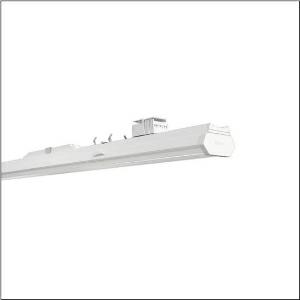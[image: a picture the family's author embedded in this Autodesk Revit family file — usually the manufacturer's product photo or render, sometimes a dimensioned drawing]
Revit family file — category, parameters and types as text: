
# Revit family: licross_21_protected_mo_52td1bvn45xgd
name_source: partatom
category: Lighting Fixtures
units: mm (PartAtom-declared; Revit-internal decimal feet)

## family parameters
Cut with Voids When Loaded = No
Host = Face
Light Source = No
Part Type = Normal
Room Calculation Point = No
Round Connector Dimension = Use Diameter
Shared = No

## types (1)
- --- (1 x LED, 5000 lm, 29.3 W, 4000K)
    Apparent Load = 29 VA
    CIE Flux Codes = 54 82 95 97 100
    Color Rendering = 80
    Color Temperature = 4000K
    Default Elevation = 1800 mm
    Description = Licross 21 Protected MO, luminaire insert, of sheet steel, galvanised, coil coated, white, length: 1.500mm, width: 90mm, height: 101mm, LED rated luminous flux: 5.000lm, light colour: 840, SDCM (Standard Deviation of Colour Matching)MacAdam ≤ 3 SDCM (initial), control gear: DALI 2, CLO (for two DALI lines), with plug, 6-pole, with phase selection, mains connection: 220..240V, AC/DC, 0/50..60Hz, start of lifetime: 29W, end of service life: 33W, internal wiring halogen-free, for central battery installations according to EN 60598-2-22, for emergency light function, without changeover relay, primary optical cover: cover, of PMMA, light emission: direct distribution, primary light characteristic: symmetric, protection rating (complete): IP54, insulation class (complete): insulation class I (protective earthing), certification: CE, ENEC, VDE, UKCA, protection symbol: D if used in an environment with non-conductive dust loads with corresponding accessories, impact resistance: IK06, permissible ambient temperature for indoor applications: -25..+50°C, standard: EN 60598-2-22, corresponds to IFS (International Featured Standards) requirements for safety and quality in the food industry, reducing of maximum allowable ambient temperature of 5°C with ceiling mounting, LABS conformity tested according to VDMA 24364:2018-05, The light source and the operating device comply with the requirements of the Ecodesign Regulation (EU) 2019/2020 and are replaceable in accordance with this regulation, packaging unit: 1 piece
    Height = 92 mm
    Lamp = 1 x LED
    Lamp Light Flux = 5000 lm
    Lamp Power = 29.3 W
    Lamp count = 1
    Length = 1500 mm
    Luminous efficacy = 171 lm/W
    Manufacturer = Siteco
    ModVariant = No
    Model = 52TD1BVN45XGD
    Mounting Place = Ceiling
    Mounting Type = Pendant
    Number of Poles = 1
    OnlyDefault = Yes
    Power Factor = 1
    Product Name = Licross 21 Protected MO
    Product group = luminaire insert | ceiling pendant
    ProductGroupID = 901
    Protection Class = Protection class I
    Protection Degree = IP 54
    RLX_Detail_Level = 1
    RLX_Emergency_Light_Flux = 0 lm
    RLX_Emergency_Type = 0
    RLX_Emergency_Type_DB = No
    RlxData = <blob elided: 24605 chars, md5=dd18b237>
    Socket = socket
    Standby Power = 0 W
    System Light Flux = 5000 lm
    System Power = 29 W
    Type Comments = : AC-mode, luminous flux: 100 % | dim-lin: 254 | 199 mA
    Type Image = l_1256148.jpg
    URL = http://relux.com
    VarID = @adj_103021
    Voltage = 0 V
    Weight = 0.00 kg
    Width = 88 mm

## geometry (parser evidence)
native form markers: Blend x4, Sweep x8
no freeform markers — native parametric forms only
